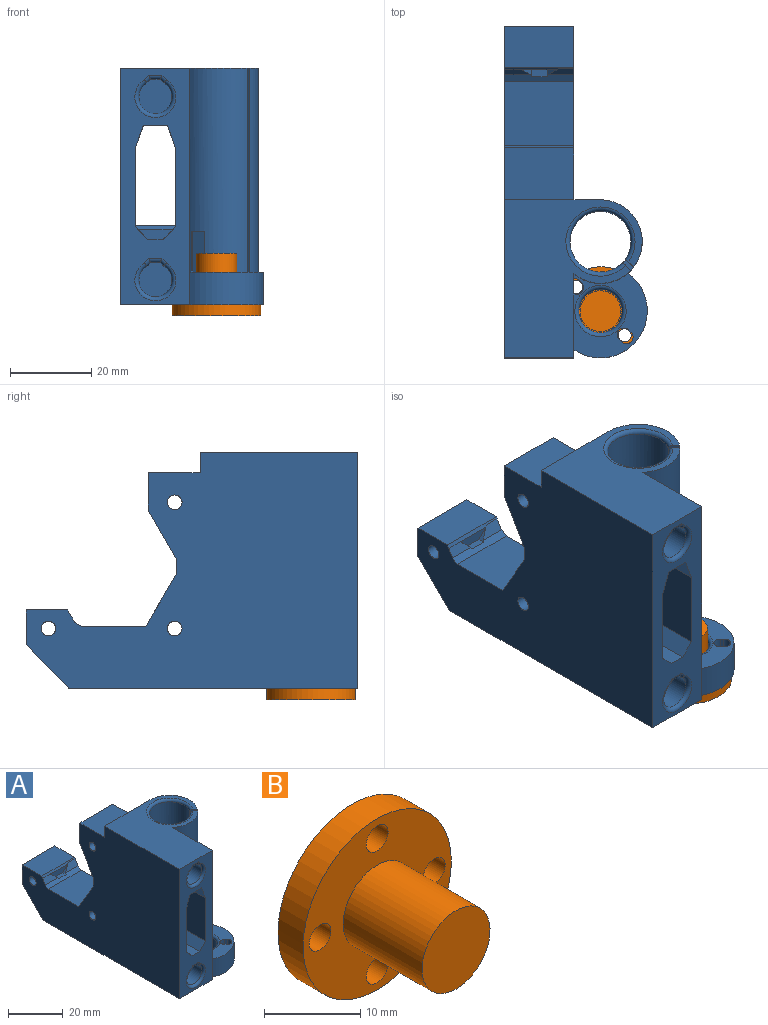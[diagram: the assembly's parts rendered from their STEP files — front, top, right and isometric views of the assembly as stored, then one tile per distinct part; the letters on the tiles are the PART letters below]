
ASSEMBLY  parts=2 mates=1
PART A: 92 faces, bbox 36.1x82.6x59.1 mm
  f0: cylinder r=1.8mm len=14mm, axis (-1,0,0), area 153.3mm2, adj f4,f28,f43,f44,f45,f78
  f1: cylinder r=1.8mm len=14mm, axis (-1,0,0), area 147.2mm2, adj f3,f8,f9,f10,f28,f76
  f2: cylinder r=1.8mm len=14mm, axis (-1,0,0), area 158.3mm2, adj f28,f74
  f3: plane 5.36x3.86mm, normal (0,0,1), area 20.7mm2, adj f1,f8,f10,f65
  f4: plane 44.58x5.91mm, normal (0,0,-1), area 263.4mm2, adj f0,f11,f43,f45
  f5: plane 2.44x2.44mm, normal (-0.71,0,0.71), area 2.5mm2, adj f6,f58,f67,f71
  f6: plane 3.86x1.74mm, normal (0,0,1), area 6.7mm2, adj f5,f7,f67,f71
  f7: plane 2.44x2.44mm, normal (0.71,0,0.71), area 2.5mm2, adj f6,f67,f68,f71
  f8: plane 52.76x4.17mm, normal (-0.71,0,0.71), area 219.1mm2, adj f1,f3,f9,f11,f46,f65
  f9: plane 43.71x3.86mm, normal (0,0,1), area 168.6mm2, adj f1,f8,f10,f11
  f10: plane 52.76x4.17mm, normal (0.71,0,0.71), area 219.1mm2, adj f1,f3,f9,f11,f47,f65
  f11: plane 58x17mm, normal (0,-1,0), area 563.9mm2, adj f4,f8,f9,f10,f15,f22,f28,f31
  f12: plane 17x0.25mm, normal (-0.01,1,0), area 2.2mm2, adj f25,f31,f73
  f13: cylinder r=10.25mm len=58mm, axis (0,0,-1), area 2066.6mm2, adj f15,f22,f23,f24,f30,f31,f32,f33
  f14: cylinder r=7.49mm len=56mm, axis (0,0,-1), area 2580.4mm2, adj f32,f33,f34,f88,f90
  f15: plane 38.75x33.75mm, normal (0,0,1), area 723.8mm2, adj f11,f13,f22,f24,f28,f33,f34,f88
  f16: cylinder r=1.65mm len=8mm, axis (0,0,-1), area 41.5mm2, adj f17,f29,f30,f31
  f17: plane 8x0.57mm, normal (-0.71,-0.71,0), area 6.4mm2, adj f16,f18,f30,f31
  f18: cylinder r=1.65mm len=8mm, axis (0,0,-1), area 41.5mm2, adj f17,f29,f30,f31
  f19: cylinder r=1.65mm len=8mm, axis (0,0,-1), area 41.5mm2, adj f20,f26,f30,f31
  f20: plane 8x0.57mm, normal (-0.71,-0.71,0), area 6.4mm2, adj f19,f21,f30,f31
  f21: cylinder r=1.65mm len=8mm, axis (0,0,-1), area 41.5mm2, adj f20,f26,f30,f31
  f22: plane 58x20.57mm, normal (1,0,0), area 987.1mm2, adj f11,f13,f15,f23,f30,f31,f36,f37
  f23: cylinder r=11.5mm len=20.8mm, axis (0,0,-1), area 286.4mm2, adj f13,f22,f30,f31
  f24: plane 58x23.5mm, normal (0,1,0), area 462.2mm2, adj f13,f15,f25,f28,f31,f61
  f25: plane 52.99x42.75mm, normal (1,0,0), area 923.1mm2, adj f12,f24,f31,f58,f59,f60,f61,f62
  f26: plane 8x0.57mm, normal (0.71,0.71,0), area 6.4mm2, adj f19,f21,f30,f31
  f27: cylinder r=5.3mm len=10.6mm, axis (0,0,-1), area 199.8mm2, adj f89,f91
  f28: plane 81.5x58mm, normal (-1,0,0), area 3230.7mm2, adj f0,f1,f2,f11,f15,f24,f31,f61
  f29: plane 8x0.57mm, normal (0.71,0.71,0), area 6.4mm2, adj f16,f18,f30,f31
  f30: plane 20.8x20.15mm, normal (0,0,1), area 169.2mm2, adj f13,f16,f17,f18,f19,f20,f21,f22
  f31: plane 71.05x35mm, normal (0,0,-1), area 1430.5mm2, adj f11,f12,f13,f16,f17,f18,f19,f20
  f32: plane 2.77x2.56mm, normal (0,0,1), area 2.8mm2, adj f13,f14,f33,f34
  f33: plane 56.02x2.14mm, normal (-0.64,-0.77,0), area 154.4mm2, adj f13,f14,f15,f32,f88
  f34: plane 56.02x2.14mm, normal (0.64,0.77,0), area 154.4mm2, adj f13,f14,f15,f32,f88
  f35: plane 10x3.29mm, normal (1,0,0), area 32.9mm2, adj f30,f36,f37,f38
  f36: plane 5.77x2.15mm, normal (0,0,-1), area 9.7mm2, adj f22,f35,f37,f38
  f37: plane 10x2.15mm, normal (0.5,0.87,0), area 24.8mm2, adj f22,f30,f35,f36
  f38: plane 10x2.15mm, normal (0.5,-0.87,0), area 24.8mm2, adj f22,f30,f35,f36
  f39: plane 3.27x1.91mm, normal (0,0,-1), area 1.5mm2, adj f13,f40,f41,f42
  f40: plane 10x0.26mm, normal (-1,0,0), area 2.6mm2, adj f13,f30,f39,f42
  f41: plane 10x0.42mm, normal (0.5,-0.87,0), area 4.8mm2, adj f13,f30,f39,f42
  f42: plane 10x2.85mm, normal (-0.5,-0.87,0), area 32.9mm2, adj f30,f39,f40,f41
  f43: plane 51.54x5.66mm, normal (0.94,0,-0.34), area 298.8mm2, adj f0,f4,f11,f44,f47,f62,f63
  f44: plane 6.09x5.91mm, normal (0,0,-1), area 36mm2, adj f0,f43,f45,f62
  f45: plane 51.54x5.66mm, normal (-0.94,0,-0.34), area 298.8mm2, adj f0,f4,f11,f44,f46,f59,f62
  f46: plane 49.87x19.31mm, normal (-1,0,0), area 896.9mm2, adj f8,f11,f45,f59,f60,f65
  f47: plane 49.87x19.31mm, normal (1,0,0), area 896.9mm2, adj f10,f11,f43,f63,f64,f65
  f48: plane 36x0.87mm, normal (-0.71,0,-0.71), area 44.5mm2, adj f49,f51,f52,f80
  f49: cylinder r=4.04mm len=36mm, axis (0,-1,0), area 756.7mm2, adj f48,f50,f52,f82
  f50: plane 36x0.87mm, normal (0.71,0,-0.71), area 44.5mm2, adj f49,f51,f52,f83
  f51: plane 36x2.39mm, normal (0,0,-1), area 86mm2, adj f48,f50,f52,f81
  f52: plane 8.38x8.07mm, normal (0,-1,0), area 52.4mm2, adj f48,f49,f50,f51
  f53: plane 36x0.87mm, normal (-0.71,0,-0.71), area 44.5mm2, adj f54,f56,f57,f84
  f54: cylinder r=4.04mm len=36mm, axis (0,-1,0), area 756.7mm2, adj f53,f55,f57,f86
  f55: plane 36x0.87mm, normal (0.71,0,-0.71), area 44.5mm2, adj f54,f56,f57,f87
  f56: plane 36x2.39mm, normal (0,0,-1), area 86mm2, adj f53,f55,f57,f85
  f57: plane 8.38x8.07mm, normal (0,-1,0), area 52.4mm2, adj f53,f54,f55,f56
  f58: plane 6.3x2.6mm, normal (0,-0.86,0.51), area 14.8mm2, adj f5,f25,f67,f69
  f59: plane 12.1x6.99mm, normal (0,0.87,-0.5), area 55.2mm2, adj f25,f45,f46,f60,f62
  f60: plane 3.5x3.49mm, normal (0,1,0), area 12.2mm2, adj f25,f46,f59,f65
  f61: plane 17x12.76mm, normal (0,0,1), area 216.9mm2, adj f24,f25,f28,f62
  f62: plane 17x9.14mm, normal (0,1,0), area 154.5mm2, adj f25,f28,f43,f44,f45,f59,f61,f63
  f63: plane 12.1x6.99mm, normal (0,0.87,-0.5), area 55.2mm2, adj f28,f43,f47,f62,f64
  f64: plane 3.5x3.49mm, normal (0,1,0), area 12.2mm2, adj f28,f47,f63,f65
  f65: plane 17x13.01mm, normal (0,0.86,0.5), area 124.8mm2, adj f3,f8,f10,f25,f28,f46,f47,f60
  f66: plane 17x15.72mm, normal (0,0,1), area 267.3mm2, adj f25,f28,f65,f67
  f67: plane 17x1.73mm, normal (0,-0.51,0.86), area 31.8mm2, adj f5,f6,f7,f25,f28,f58,f66,f68
  f68: plane 6.3x2.26mm, normal (0,-0.86,0.51), area 13.3mm2, adj f7,f28,f67,f69
  f69: plane 17.01x0.88mm, normal (0,-0.87,0.5), area 15.1mm2, adj f25,f28,f58,f68,f70,f71
  f70: plane 17x10.2mm, normal (0,0,1), area 173.3mm2, adj f25,f28,f69,f72
  f71: plane 8.73x2.44mm, normal (0,-1,0), area 15.3mm2, adj f5,f6,f7,f69
  f72: plane 17x8.43mm, normal (0,1,0), area 143.3mm2, adj f25,f28,f70,f73
  f73: plane 17x10.88mm, normal (0,0.71,-0.7), area 256.3mm2, adj f12,f25,f28,f72
  f74: plane 6.2x6.2mm, normal (1,0,0), area 20mm2, adj f2,f75
  f75: cylinder r=3.1mm len=6.2mm, axis (1,0,0), area 58.4mm2, adj f25,f74
  f76: plane 6.2x6.2mm, normal (1,0,0), area 20mm2, adj f1,f77
  f77: cylinder r=3.1mm len=6.2mm, axis (1,0,0), area 58.4mm2, adj f25,f76
  f78: plane 6.2x6.2mm, normal (1,0,0), area 20mm2, adj f0,f79
  f79: cylinder r=3.1mm len=6.2mm, axis (1,0,0), area 58.4mm2, adj f25,f78
  f80: cylinder r=1mm len=1.87mm, axis (0.71,0,-0.71), area 2.2mm2, adj f11,f48,f81,f82
  f81: cylinder r=1mm len=3.22mm, axis (1,0,0), area 4.4mm2, adj f11,f51,f80,f83
  f82: torus R=5.04mm, axis (0,-1,0), area 35.8mm2, adj f11,f49,f80,f83
  f83: cylinder r=1mm len=1.87mm, axis (0.71,0,0.71), area 2.2mm2, adj f11,f50,f81,f82
  f84: cylinder r=1mm len=1.87mm, axis (0.71,0,-0.71), area 2.2mm2, adj f11,f53,f85,f86
  f85: cylinder r=1mm len=3.22mm, axis (1,0,0), area 4.4mm2, adj f11,f56,f84,f87
  f86: torus R=5.04mm, axis (0,-1,0), area 35.8mm2, adj f11,f54,f84,f87
  f87: cylinder r=1mm len=1.87mm, axis (0.71,0,0.71), area 2.2mm2, adj f11,f55,f85,f86
  f88: torus R=8.49mm, axis (0,0,1), area 76mm2, adj f14,f15,f33,f34
  f89: torus R=6.3mm, axis (0,0,1), area 55.9mm2, adj f27,f31
  f90: torus R=8.49mm, axis (0,0,1), area 77.5mm2, adj f14,f31
  f91: torus R=6.3mm, axis (0,0,1), area 55.9mm2, adj f27,f30
PART B: 9 faces, bbox 21.8x15.3x21.8 mm
  f0: cylinder r=1.6mm len=3.7mm, axis (0,1,0), area 37.2mm2, adj f5,f6
  f1: cylinder r=1.6mm len=3.7mm, axis (0,1,0), area 37.2mm2, adj f5,f6
  f2: cylinder r=1.6mm len=3.7mm, axis (0,1,0), area 37.2mm2, adj f5,f6
  f3: cylinder r=1.6mm len=3.7mm, axis (0,1,0), area 37.2mm2, adj f5,f6
  f4: cylinder r=10.9mm len=21.8mm, axis (0,1,0), area 253.4mm2, adj f5,f6
  f5: plane 21.8x21.8mm, normal (0,-1,0), area 262.5mm2, adj f0,f1,f2,f3,f4,f7
  f6: plane 21.8x21.8mm, normal (0,1,0), area 341.1mm2, adj f0,f1,f2,f3,f4
  f7: cylinder r=5mm len=11.6mm, axis (0,1,0), area 364.4mm2, adj f5,f8
  f8: plane 10x10mm, normal (0,-1,0), area 78.5mm2, adj f7
PLACE A at identity fixed
PLACE B rot(axis=(-0.86,0.36,-0.36),98.5deg) t=(49.44,-1.69,-42.9)mm
MATE revolute A.f89 <-> B.f4  axis (0,0,-1) through (5.44,42.5,-39.2)mm
